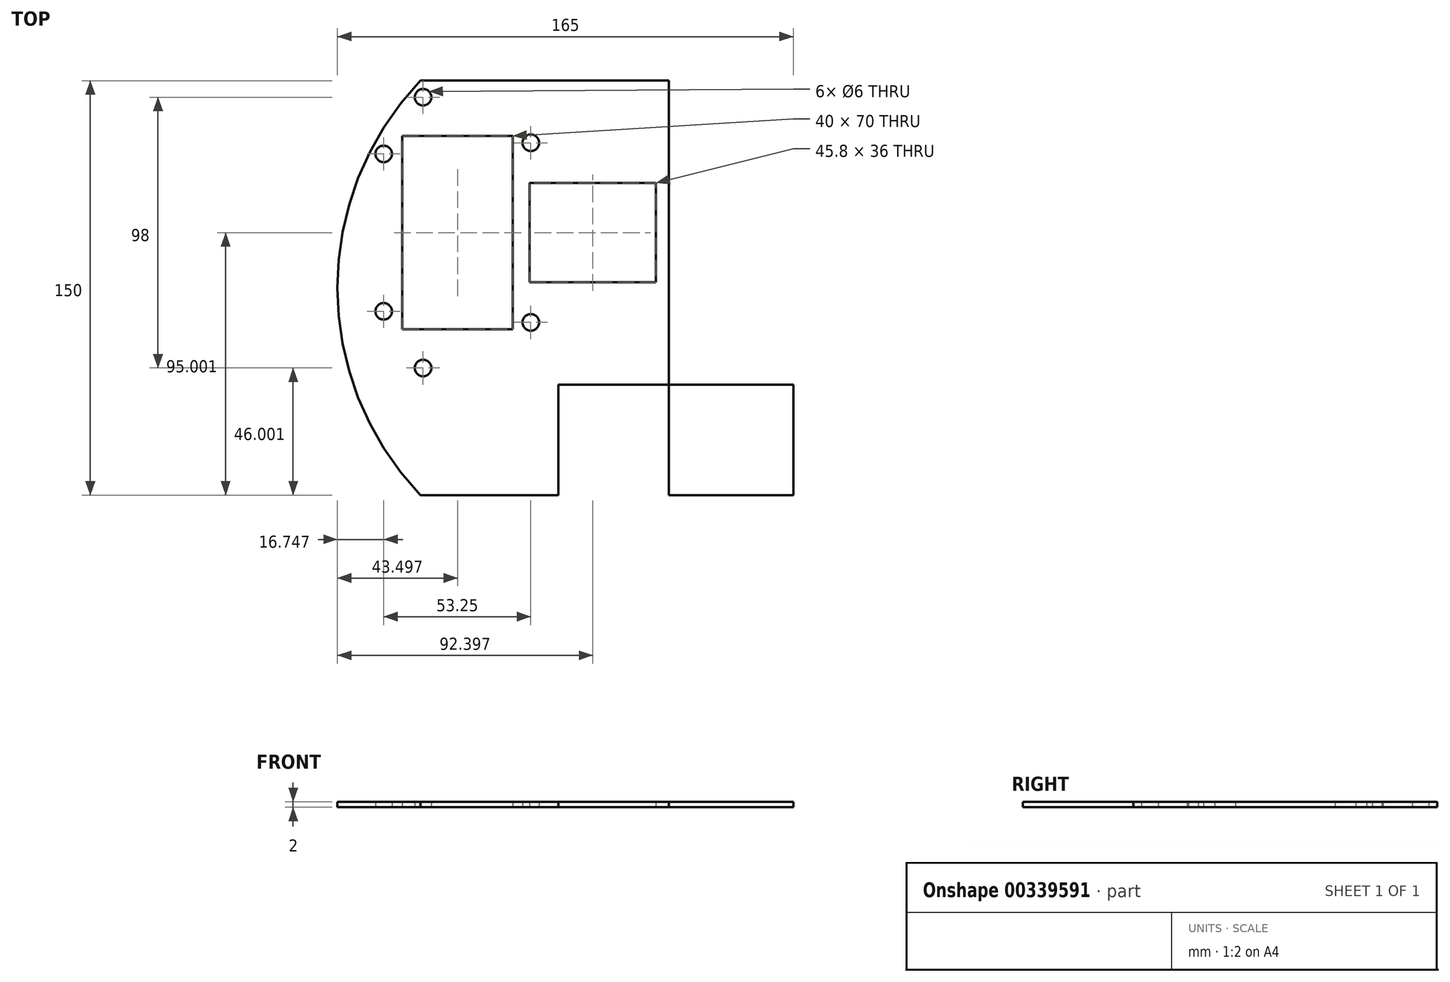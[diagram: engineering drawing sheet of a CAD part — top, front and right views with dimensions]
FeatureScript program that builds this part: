
annotation { "Feature Type Name" : "Feature", "Feature Type Description" : "" }
export const myFeature = defineFeature(function(context is Context, id is Id, definition is map)
    precondition{}
    {
        {
            var Q0;
            Q0=qCreatedBy(makeId("Top.planeOp"),FACE);
            var sketch = newSketch(context, id + "F0", { "sketchPlane" : qUnion([Q0])});
            skLineSegment(sketch, "E0.bottom", {"start": v(-100.74, 74.34) * mm, "end": v(-10.74, 74.34) * mm});
            skLineSegment(sketch, "E0.top", {"start": v(-100.74, -75.66) * mm, "end": v(-10.74, -75.66) * mm});
            skLineSegment(sketch, "E0.left", {"start": v(-100.74, 74.34) * mm, "end": v(-100.74, -75.66) * mm});
            skLineSegment(sketch, "E0.right", {"start": v(-10.74, 74.34) * mm, "end": v(-10.74, -75.66) * mm});
            skArc(sketch, "E1", {"start": v(-100.74, 74.34) * mm, "mid": v(-130.74, -0.66) * mm, "end": v(-100.74, -75.66) * mm});
            skLineSegment(sketch, "E2.bottom", {"start": v(-107.24, 54.34) * mm, "end": v(-67.24, 54.34) * mm});
            skLineSegment(sketch, "E2.top", {"start": v(-107.24, -15.66) * mm, "end": v(-67.24, -15.66) * mm});
            skLineSegment(sketch, "E2.left", {"start": v(-107.24, 54.34) * mm, "end": v(-107.24, -15.66) * mm});
            skLineSegment(sketch, "E2.right", {"start": v(-67.24, 54.34) * mm, "end": v(-67.24, -15.66) * mm});
            skLineSegment(sketch, "E3.bottom", {"start": v(-61.24, 37.34) * mm, "end": v(-15.44, 37.34) * mm});
            skLineSegment(sketch, "E3.top", {"start": v(-61.24, 1.34) * mm, "end": v(-15.44, 1.34) * mm});
            skLineSegment(sketch, "E3.left", {"start": v(-61.24, 37.34) * mm, "end": v(-61.24, 1.34) * mm});
            skLineSegment(sketch, "E3.right", {"start": v(-15.44, 37.34) * mm, "end": v(-15.44, 1.34) * mm});
            skLineSegment(sketch, "E4.MirrorCS", {"start": v(79.26, 74.34) * mm, "end": v(79.26, -75.66) * mm});
            skArc(sketch, "E5.MirrorCS", {"start": v(79.26, 74.34) * mm, "mid": v(109.26, -0.66) * mm, "end": v(79.26, -75.66) * mm});
            skLineSegment(sketch, "E6.MirrorCS", {"start": v(85.76, 54.34) * mm, "end": v(45.76, 54.34) * mm});
            skLineSegment(sketch, "E7.MirrorCS", {"start": v(85.76, -15.66) * mm, "end": v(45.76, -15.66) * mm});
            skLineSegment(sketch, "E8.MirrorCS", {"start": v(79.26, -75.66) * mm, "end": v(-10.74, -75.66) * mm});
            skLineSegment(sketch, "E9.MirrorCS", {"start": v(85.76, 54.34) * mm, "end": v(85.76, -15.66) * mm});
            skLineSegment(sketch, "E10.MirrorCS", {"start": v(45.76, 54.34) * mm, "end": v(45.76, -15.66) * mm});
            skLineSegment(sketch, "E11.MirrorCS", {"start": v(39.76, 37.34) * mm, "end": v(-6.04, 37.34) * mm});
            skLineSegment(sketch, "E12.MirrorCS", {"start": v(39.76, 1.34) * mm, "end": v(-6.04, 1.34) * mm});
            skLineSegment(sketch, "E13.MirrorCS", {"start": v(39.76, 37.34) * mm, "end": v(39.76, 1.34) * mm});
            skLineSegment(sketch, "E14.MirrorCS", {"start": v(-6.04, 37.34) * mm, "end": v(-6.04, 1.34) * mm});
            skLineSegment(sketch, "E15.MirrorCS", {"start": v(79.26, 74.34) * mm, "end": v(-10.74, 74.34) * mm});
            skPoint(sketch, "E16", {"position": v(-67.24, 19.34) * mm});
            skPoint(sketch, "E17", {"position": v(-61.24, 19.34) * mm});
            skCircle(sketch, "E18", {"center": v(-99.74, -29.66) * mm, "radius": 3 * mm});
            skCircle(sketch, "E19", {"center": v(-114, -9.16) * mm, "radius": 3 * mm});
            skPoint(sketch, "E20", {"position": v(-107.24, 19.34) * mm});
            skLineSegment(sketch, "E21", {"start": v(-107.24, 19.34) * mm, "end": v(-67.24, 19.34) * mm});
            skCircle(sketch, "E22", {"center": v(-114, 47.84) * mm, "radius": 3 * mm});
            skCircle(sketch, "E23", {"center": v(-99.74, 68.34) * mm, "radius": 3 * mm});
            skPoint(sketch, "E24.MirrorP", {"position": v(85.76, 19.34) * mm});
            skLineSegment(sketch, "E25.MirrorCS", {"start": v(85.76, 19.34) * mm, "end": v(45.76, 19.34) * mm});
            skPoint(sketch, "E26.MirrorP", {"position": v(39.76, 19.34) * mm});
            skCircle(sketch, "E27.MirrorC", {"center": v(78.26, 68.34) * mm, "radius": 3 * mm});
            skPoint(sketch, "E28.MirrorP", {"position": v(45.76, 19.34) * mm});
            skCircle(sketch, "E29.MirrorC", {"center": v(92.5, -9.16) * mm, "radius": 3 * mm});
            skCircle(sketch, "E30.MirrorC", {"center": v(78.26, -29.66) * mm, "radius": 3 * mm});
            skCircle(sketch, "E31.MirrorC", {"center": v(92.5, 47.84) * mm, "radius": 3 * mm});
            skCircle(sketch, "E32", {"center": v(-60.74, 51.84) * mm, "radius": 3 * mm});
            skCircle(sketch, "E33", {"center": v(-60.74, -13.16) * mm, "radius": 3 * mm});
            skCircle(sketch, "E34.MirrorC", {"center": v(39.26, -13.16) * mm, "radius": 3 * mm});
            skCircle(sketch, "E35.MirrorC", {"center": v(39.26, 51.84) * mm, "radius": 3 * mm});
            skLineSegment(sketch, "E36.bottom", {"start": v(-10.74, -75.66) * mm, "end": v(-50.74, -75.66) * mm});
            skLineSegment(sketch, "E36.top", {"start": v(-10.74, -35.66) * mm, "end": v(-50.74, -35.66) * mm});
            skLineSegment(sketch, "E36.left", {"start": v(-10.74, -75.66) * mm, "end": v(-10.74, -35.66) * mm});
            skLineSegment(sketch, "E36.right", {"start": v(-50.74, -75.66) * mm, "end": v(-50.74, -35.66) * mm});
            skLineSegment(sketch, "E37.bottom", {"start": v(-10.74, -35.66) * mm, "end": v(34.26, -35.66) * mm});
            skLineSegment(sketch, "E37.top", {"start": v(-10.74, -75.66) * mm, "end": v(34.26, -75.66) * mm});
            skLineSegment(sketch, "E37.left", {"start": v(-10.74, -35.66) * mm, "end": v(-10.74, -75.66) * mm});
            skLineSegment(sketch, "E37.right", {"start": v(34.26, -35.66) * mm, "end": v(34.26, -75.66) * mm});
            skSolve(sketch);
        }
        {
            var Q0;
            {var subQ8=sQuery(id+"F0.wireOp",EDGE,"E1");Q0=makeQuery(id+"F0.imprint","IMPRINT",FACE,{"disambiguationData":[TD([[makeQuery(id+"F0.imprint","IMPRINT",EDGE,{"derivedFrom":subQ8}),1.0]])]});}
            var Q1;
            {var subQ9=sQuery(id+"F0.wireOp",EDGE,"E0.bottom");Q1=makeQuery(id+"F0.imprint","IMPRINT",FACE,{"disambiguationData":[TD([[makeQuery(id+"F0.imprint","IMPRINT",EDGE,{"derivedFrom":subQ9}),-1.0]])]});}
            var Q2;
            Q2=makeQuery(id+"F0.imprint","IMPRINT",FACE,{"disambiguationData":[TD([[makeQuery(id+"F0.imprint","IMPRINT",EDGE,{"derivedFrom":sQuery(id+"F0.wireOp",EDGE,"E0.right")}),1.0]])]});
            var Q3;
            {var subQ1=sQuery(id+"F0.wireOp",EDGE,"E5.MirrorCS");Q3=makeQuery(id+"F0.imprint","IMPRINT",FACE,{"disambiguationData":[TD([[makeQuery(id+"F0.imprint","IMPRINT",EDGE,{"derivedFrom":subQ1}),-1.0]])]});}
            extrude(context, id + "F1", {"entities" : qUnion([Q0, Q1, Q2, Q3]), "depth" : 2 * mm});
        }
    });
